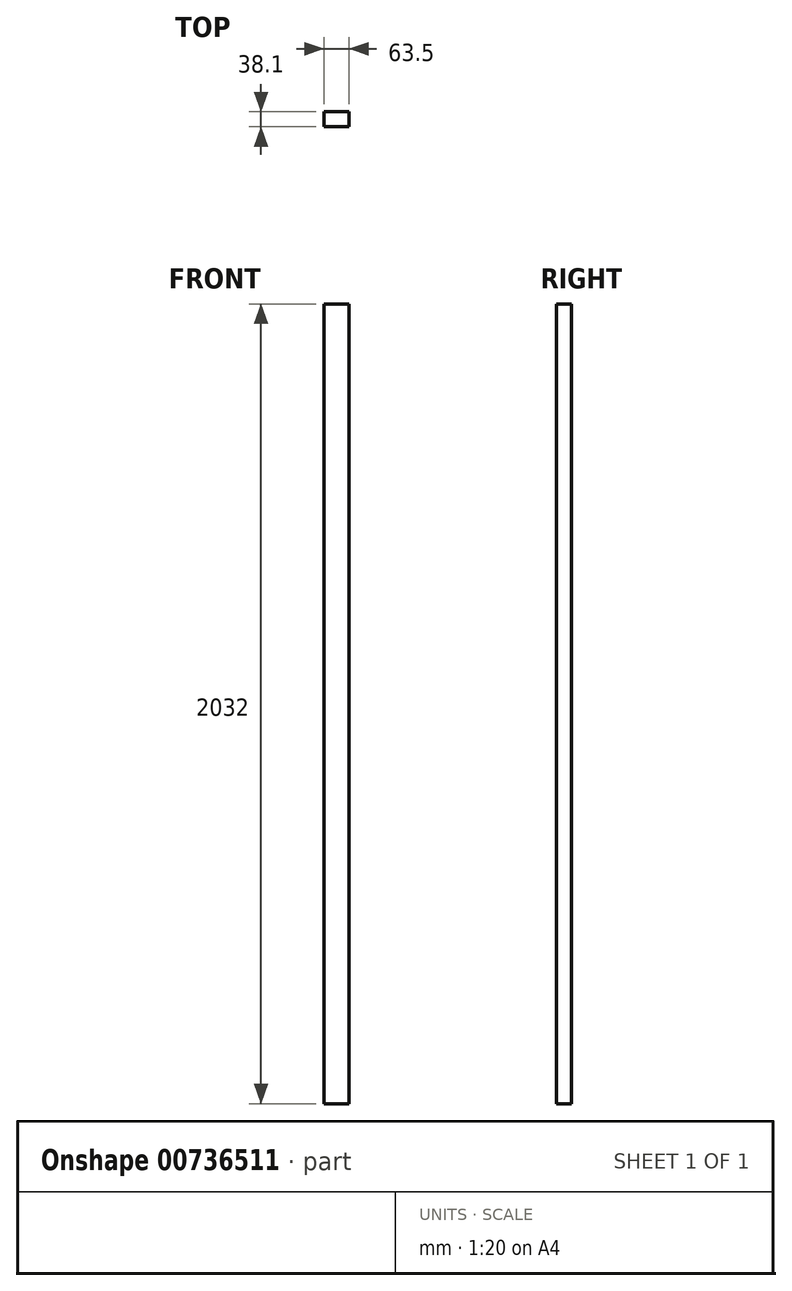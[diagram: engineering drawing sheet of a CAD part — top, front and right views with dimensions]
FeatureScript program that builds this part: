
annotation { "Feature Type Name" : "Feature", "Feature Type Description" : "" }
export const myFeature = defineFeature(function(context is Context, id is Id, definition is map)
    precondition{}
    {
        {
            var Q0;
            Q0=qCreatedBy(makeId("Top.planeOp"),FACE);
            var sketch = newSketch(context, id + "F0", { "sketchPlane" : qUnion([Q0])});
            skLineSegment(sketch, "E0.bottom", {"start": v(31.75, 19.05) * mm, "end": v(-31.75, 19.05) * mm});
            skLineSegment(sketch, "E0.top", {"start": v(31.75, -19.05) * mm, "end": v(-31.75, -19.05) * mm});
            skLineSegment(sketch, "E0.left", {"start": v(31.75, 19.05) * mm, "end": v(31.75, -19.05) * mm});
            skLineSegment(sketch, "E0.right", {"start": v(-31.75, 19.05) * mm, "end": v(-31.75, -19.05) * mm});
            skPoint(sketch, "E0.middle", {"position": v(0, 0) * mm});
            skSolve(sketch);
        }
        {
            var Q0;
            Q0 = qSketchRegion(id + "F0", true);
            extrude(context, id + "F1", {"entities" : qUnion([Q0]), "depth" : 2032 * mm, "offsetDistance" : 25.4 * mm});
        }
    });
